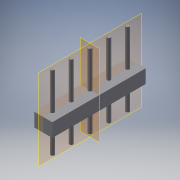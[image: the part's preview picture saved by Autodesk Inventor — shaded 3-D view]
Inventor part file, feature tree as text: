
AUTODESK INVENTOR PART (.ipt)
format: ipt  version: 2019.4 (Build 234330000, 330)  size: 124,416 bytes
history: native  units: mm
features: extrude x2, plane x2, sketch x2, pattern_linear x1, projected_geometry x1
ambient origin geometry x8: Origin, YZ Plane, XZ Plane, XY Plane, X Axis, Y Axis, Z Axis, Center Point
bodies: Solid1 (feature_tree)
feature tree (8):
  extrude  "Extrusion1"  Depth=12.65mm
  extrude  "Extrusion2"  Depth=5.0mm
  pattern_linear  "Rectangular Pattern1"  Spacing1=5.0mm  [1 undecoded]
  plane  "Work Plane1"
  plane  "Work Plane2"
  sketch  "Sketch1"  dims[d0=2.45mm d1=12.65mm]
  sketch  "Sketch2"  dims[d2=1.84mm d3=0.0mm d4=0.5mm d5=5.0mm d6=5.0mm d7=0.0mm d8=0.0mm d9=50.0mm d11=2.54mm]
  projected_geometry  "Projected Loop1"
note: 1 required parameter value undecoded (feature->parameter linkage not recoverable at this tier; creation-order binding heuristic only, values carry confidence <= 0.55)
